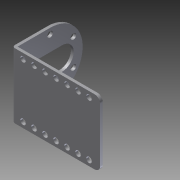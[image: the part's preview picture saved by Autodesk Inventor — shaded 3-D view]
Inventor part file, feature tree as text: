
AUTODESK INVENTOR PART (.ipt)
format: ipt  version: 2012 (Build 160160000, 160)  size: 189,440 bytes
history: native  units: mm
features: extrude x3, sketch x3, projected_geometry x1
ambient origin geometry x8: Origin, YZ Plane, XZ Plane, XY Plane, X Axis, Y Axis, Z Axis, Center Point
bodies: Solid1 (feature_tree)
feature tree (7):
  extrude  "Extrusion1"  Depth=37.59mm
  extrude  "Extrusion2"  Depth=37.59mm TaperAngle=0.0deg
  extrude  "Extrusion3"  Depth=6.35mm
  sketch  "Sketch1"  dims[d0=49.21mm d1=37.59mm]
  sketch  "Sketch3"  dims[d2=1.59mm d3=37.59mm d4=0.0mm]
  projected_geometry  "Projected Loop1"
  sketch  "Sketch4"  dims[d12=6.35mm d13=6.35mm d14=6.35mm d15=6.35mm d16=6.35mm d17=6.35mm d18=6.35mm d19=3.18mm d20=15.62mm d21=10.0mm d22=37.59mm d23=0.0mm d24=13.21mm d25=14.02mm d26=12.19mm d27=11.785mm d28=15.5mm d29=15.5mm d30=15.5mm d31=15.5mm d32=15.5mm d33=15.5mm d34=3.25mm d35=60.0mm d37=360.0deg d39=10.0mm d40=0.0mm]
